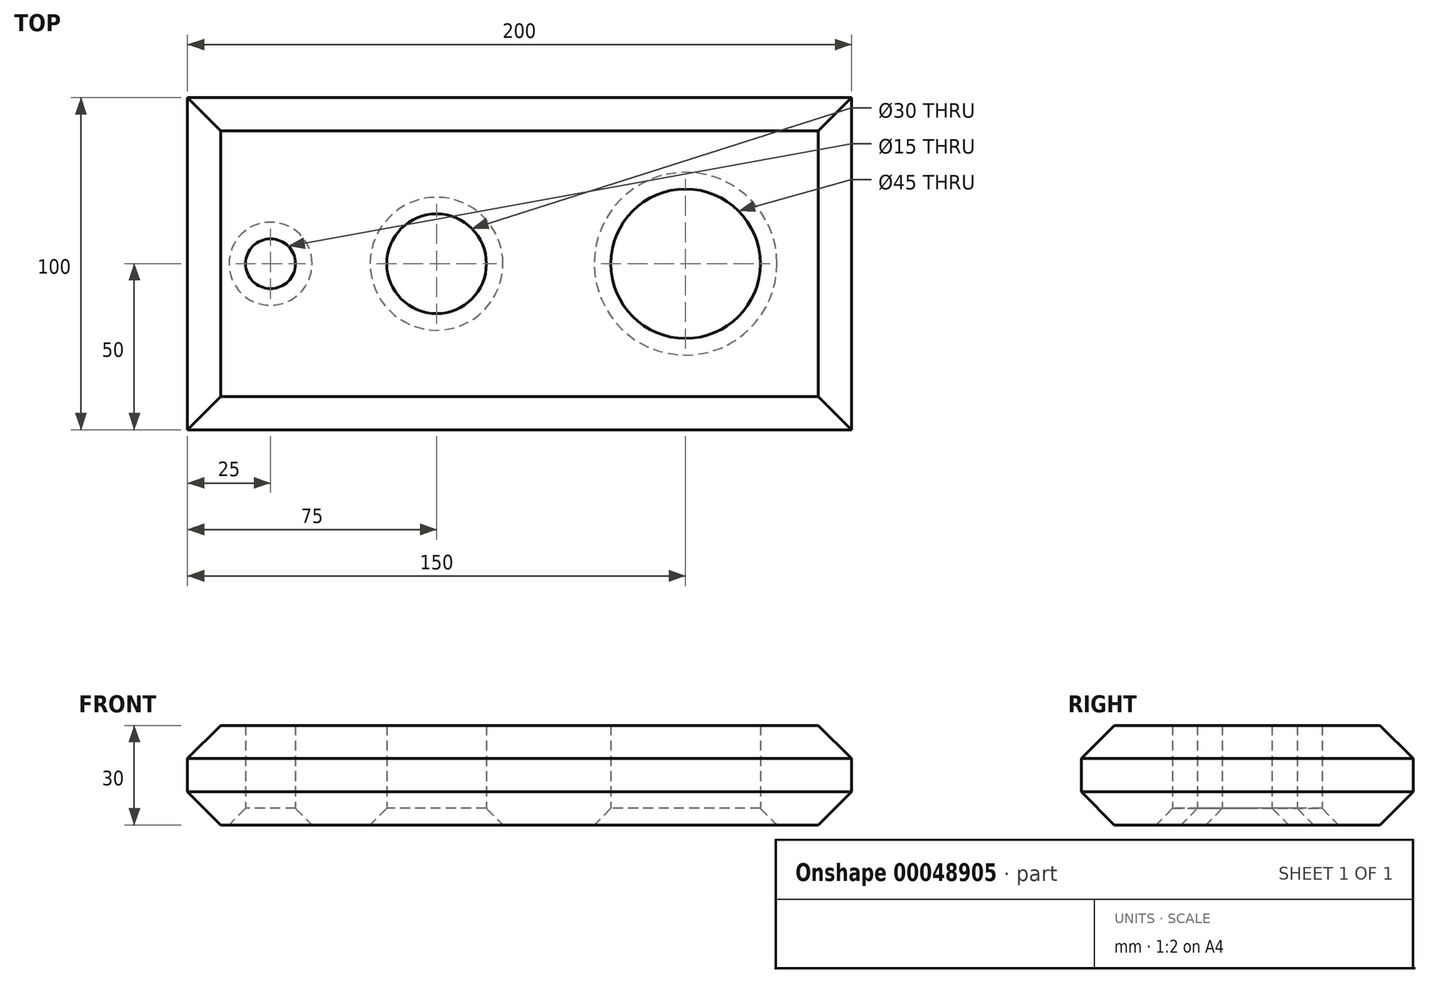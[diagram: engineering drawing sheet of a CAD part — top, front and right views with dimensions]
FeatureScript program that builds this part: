
annotation { "Feature Type Name" : "Feature", "Feature Type Description" : "" }
export const myFeature = defineFeature(function(context is Context, id is Id, definition is map)
    precondition{}
    {
        {
            var Q0;
            Q0=qCreatedBy(makeId("Top.planeOp"),FACE);
            var sketch = newSketch(context, id + "F0", { "sketchPlane" : qUnion([Q0])});
            skLineSegment(sketch, "E0.rect.bottom", {"start": v(-100, 50) * mm, "end": v(100, 50) * mm});
            skLineSegment(sketch, "E0.rect.top", {"start": v(-100, -50) * mm, "end": v(100, -50) * mm});
            skLineSegment(sketch, "E0.rect.left", {"start": v(-100, 50) * mm, "end": v(-100, -50) * mm});
            skLineSegment(sketch, "E0.rect.right", {"start": v(100, 50) * mm, "end": v(100, -50) * mm});
            skPoint(sketch, "E0.rect.middle", {"position": v(0, 0) * mm});
            skCircle(sketch, "E1", {"center": v(-75, 0) * mm, "radius": 7.5 * mm});
            skCircle(sketch, "E2", {"center": v(-25, 0) * mm, "radius": 15 * mm});
            skCircle(sketch, "E3", {"center": v(50, 0) * mm, "radius": 22.5 * mm});
            skPoint(sketch, "E4.endSnap0", {"position": v(-100, 0) * mm});
            skLineSegment(sketch, "E5", {"start": v(-100, 0) * mm, "end": v(100, 0) * mm});
            skSolve(sketch);
        }
        {
            var Q0;
            {var subQ14=sQuery(id+"F0.wireOp",EDGE,"E0.rect.bottom");Q0=makeQuery(id+"F0.imprint","IMPRINT",FACE,{"disambiguationData":[TD([[makeQuery(id+"F0.imprint","IMPRINT",EDGE,{"derivedFrom":subQ14}),-1.0]])]});}
            var Q1;
            {var subQ7=sQuery(id+"F0.wireOp",EDGE,"E0.rect.top");Q1=makeQuery(id+"F0.imprint","IMPRINT",FACE,{"disambiguationData":[TD([[makeQuery(id+"F0.imprint","IMPRINT",EDGE,{"derivedFrom":subQ7}),1.0]])]});}
            extrude(context, id + "F1", {"entities" : qUnion([Q0, Q1]), "depth" : 30 * mm});
        }
        {
            var Q0;
            Q0=makeQuery(id+"F1.opExtrude","CAP_EDGE",EDGE,{"disambiguationData":[OSD([sQuery(id+"F0.wireOp",EDGE,"E0.rect.left")])],"isStart":false});
            var Q1;
            Q1=makeQuery(id+"F1.opExtrude","CAP_EDGE",EDGE,{"disambiguationData":[OSD([sQuery(id+"F0.wireOp",EDGE,"E0.rect.left")])],"isStart":true});
            var Q2;
            Q2=makeQuery(id+"F1.opExtrude","CAP_EDGE",EDGE,{"disambiguationData":[OSD([sQuery(id+"F0.wireOp",EDGE,"E0.rect.right")])],"isStart":false});
            var Q3;
            Q3=makeQuery(id+"F1.opExtrude","CAP_EDGE",EDGE,{"disambiguationData":[OSD([sQuery(id+"F0.wireOp",EDGE,"E0.rect.right")])],"isStart":true});
            var Q4;
            Q4=makeQuery(id+"F1.opExtrude","CAP_EDGE",EDGE,{"disambiguationData":[OSD([sQuery(id+"F0.wireOp",EDGE,"E0.rect.top")])],"isStart":false});
            var Q5;
            Q5=makeQuery(id+"F1.opExtrude","CAP_EDGE",EDGE,{"disambiguationData":[OSD([sQuery(id+"F0.wireOp",EDGE,"E0.rect.bottom")])],"isStart":false});
            var Q6;
            Q6=makeQuery(id+"F1.opExtrude","CAP_EDGE",EDGE,{"disambiguationData":[OSD([sQuery(id+"F0.wireOp",EDGE,"E0.rect.top")])],"isStart":true});
            var Q7;
            Q7=makeQuery(id+"F1.opExtrude","CAP_EDGE",EDGE,{"disambiguationData":[OSD([sQuery(id+"F0.wireOp",EDGE,"E0.rect.bottom")])],"isStart":true});
            chamfer(context, id + "F2", {"entities" : qUnion([Q0, Q1, Q2, Q3, Q4, Q5, Q6, Q7]), "chamferType" : ChamferType.OFFSET_ANGLE, "width" : 10 * mm, "oppositeDirection" : false, "angle" : 45 * degree, "tangentPropagation" : true});
        }
        {
            var Q0;
            Q0=makeQuery(id+"F1.opExtrude","CAP_EDGE",EDGE,{"disambiguationData":[OSD([sQuery(id+"F0.wireOp",EDGE,"E1")])],"isStart":true});
            var Q1;
            Q1=makeQuery(id+"F1.opExtrude","CAP_EDGE",EDGE,{"disambiguationData":[OSD([sQuery(id+"F0.wireOp",EDGE,"E2")])],"isStart":true});
            var Q2;
            Q2=makeQuery(id+"F1.opExtrude","CAP_EDGE",EDGE,{"disambiguationData":[OSD([sQuery(id+"F0.wireOp",EDGE,"E3")])],"isStart":true});
            chamfer(context, id + "F3", {"entities" : qUnion([Q0, Q1, Q2]), "width" : 5 * mm, "tangentPropagation" : true});
        }
    });
